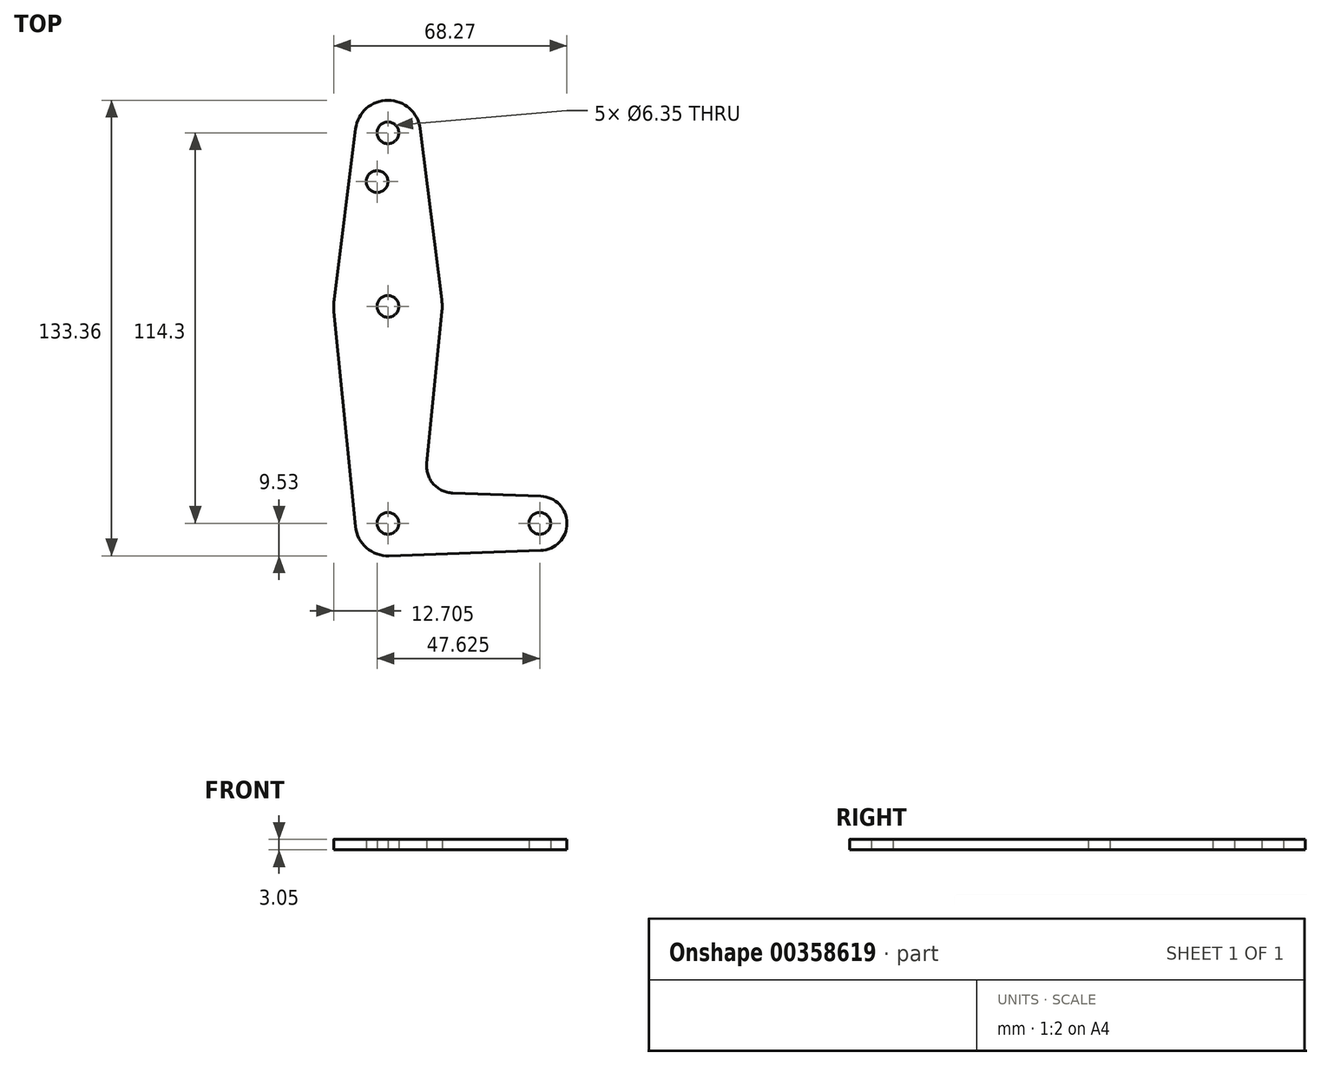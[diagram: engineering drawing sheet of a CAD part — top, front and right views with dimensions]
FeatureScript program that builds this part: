
annotation { "Feature Type Name" : "Feature", "Feature Type Description" : "" }
export const myFeature = defineFeature(function(context is Context, id is Id, definition is map)
    precondition{}
    {
        {
            var Q0;
            Q0=qCreatedBy(makeId("Top.planeOp"),FACE);
            var sketch = newSketch(context, id + "F0", { "sketchPlane" : qUnion([Q0])});
            skCircle(sketch, "E0", {"center": v(0, 0) * mm, "radius": 9.52 * mm});
            skCircle(sketch, "E1", {"center": v(0, 63.5) * mm, "radius": 15.88 * mm});
            skCircle(sketch, "E2", {"center": v(0, 114.3) * mm, "radius": 9.53 * mm});
            skCircle(sketch, "E3", {"center": v(44.45, 0) * mm, "radius": 7.94 * mm});
            skLineSegment(sketch, "E4", {"start": v(-15.8, 61.91) * mm, "end": v(-9.48, -0.95) * mm});
            skLineSegment(sketch, "E5", {"start": v(-15.75, 65.48) * mm, "end": v(-9.45, 115.5) * mm});
            skLineSegment(sketch, "E6", {"start": v(15.75, 65.48) * mm, "end": v(9.45, 115.5) * mm});
            skLineSegment(sketch, "E7", {"start": v(0.34, -9.52) * mm, "end": v(44.73, -7.94) * mm});
            skCircle(sketch, "E8", {"center": v(0, 114.3) * mm, "radius": 3.18 * mm});
            skCircle(sketch, "E9", {"center": v(0, 63.5) * mm, "radius": 3.18 * mm});
            skCircle(sketch, "E10", {"center": v(0, 0) * mm, "radius": 3.18 * mm});
            skCircle(sketch, "E11", {"center": v(44.45, 0) * mm, "radius": 3.18 * mm});
            skLineSegment(sketch, "E12", {"start": v(0, 0) * mm, "end": v(44.45, 0) * mm, "construction": true});
            skLineSegment(sketch, "E13", {"start": v(0, 0) * mm, "end": v(0, 114.3) * mm, "construction": true});
            skCircle(sketch, "E14", {"center": v(-3.18, 100.03) * mm, "radius": 3.18 * mm});
            skLineSegment(sketch, "E15", {"start": v(15.8, 61.91) * mm, "end": v(11.34, 17.6) * mm});
            skLineSegment(sketch, "E16", {"start": v(44.73, 7.94) * mm, "end": v(18.97, 8.86) * mm});
            skArc(sketch, "E17.filletArc", {"start": v(11.34, 17.6) * mm, "mid": v(13.26, 11.57) * mm, "end": v(18.97, 8.86) * mm});
            skSolve(sketch);
        }
        {
            var Q0;
            Q0=qSketchRegion(id+"F0",true);
            extrude(context, id + "F1", {"entities" : qUnion([Q0]), "depth" : 3.05 * mm});
        }
    });
